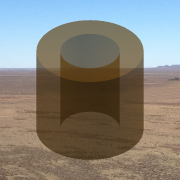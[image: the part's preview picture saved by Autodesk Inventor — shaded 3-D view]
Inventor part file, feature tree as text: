
AUTODESK INVENTOR PART (.ipt)
format: ipt  version: 2014 SP1 (Build 180222100, 222)  size: 129,536 bytes
history: native  units: in
note: dims shown in document units (in); Inventor stores cm internally (conversion verified against a paired STEP export)
features: extrude x1, sketch x1
ambient origin geometry x8: Origin, YZ Plane, XZ Plane, XY Plane, X Axis, Y Axis, Z Axis, Center Point
bodies: Solid1 (feature_tree)
feature tree (2):
  extrude  "Extrusion1"  Depth=8.0in
  sketch  "Sketch1"  dims[d0=9.0in d1=2.0in d2=8.0in d3=0.0in]
